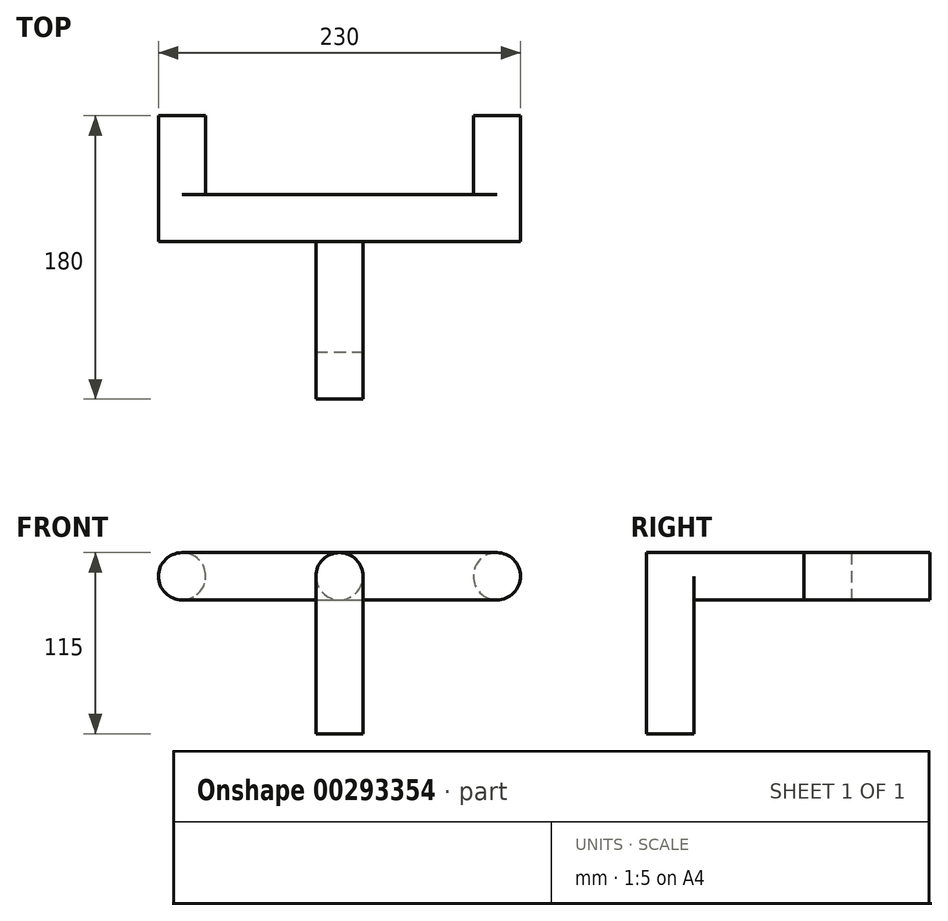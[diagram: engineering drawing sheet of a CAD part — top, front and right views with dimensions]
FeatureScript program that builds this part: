
annotation { "Feature Type Name" : "Feature", "Feature Type Description" : "" }
export const myFeature = defineFeature(function(context is Context, id is Id, definition is map)
    precondition{}
    {
        {
            var Q0;
            Q0=qCreatedBy(makeId("Front.planeOp"),FACE);
            cPlane(context, id + "F0", {"entities" : qUnion([Q0]), "cplaneType" : CPlaneType.OFFSET, "offset" : 50 * mm, "width" : 150 * mm, "height" : 150 * mm});
        }
        {
            var Q0;
            Q0=qCreatedBy(id+"F0.planeOp",FACE);
            var sketch = newSketch(context, id + "F1", { "sketchPlane" : qUnion([Q0])});
            skLineSegment(sketch, "E0", {"start": v(100, -14.73) * mm, "end": v(100, -15) * mm});
            skLineSegment(sketch, "E1.bottom", {"start": v(-100, 15) * mm, "end": v(100, 15) * mm});
            skLineSegment(sketch, "E1.top", {"start": v(-100, -15) * mm, "end": v(100, -15) * mm});
            skLineSegment(sketch, "E1.right", {"start": v(100, 15) * mm, "end": v(100, 14.73) * mm});
            skArc(sketch, "E2", {"start": v(-100, 15) * mm, "mid": v(-115, 0) * mm, "end": v(-100, -15) * mm});
            skArc(sketch, "E3", {"start": v(100, -14.73) * mm, "mid": v(114.73, 0) * mm, "end": v(100, 14.73) * mm});
            skArc(sketch, "E4", {"start": v(100, -15) * mm, "mid": v(115, 0) * mm, "end": v(100, 15) * mm});
            skLineSegment(sketch, "E5.top", {"start": v(-100, -14.73) * mm, "end": v(100, -14.73) * mm});
            skSolve(sketch);
        }
        {
            var Q0;
            Q0 = qSketchRegion(id + "F1", true);
            extrude(context, id + "F2", {"entities" : qUnion([Q0]), "depth" : 30 * mm});
        }
        {
            var Q0;
            Q0=makeQuery(id+"F2.opExtrude","CAP_FACE",FACE,{"disambiguationData":[OSD([sQuery(id+"F1.wireOp",EDGE,"E1.top"),sQuery(id+"F1.wireOp",EDGE,"E2"),sQuery(id+"F1.wireOp",EDGE,"E4"),sQuery(id+"F1.wireOp",EDGE,"E1.bottom")])],"isStart":false});
            var sketch = newSketch(context, id + "F3", { "sketchPlane" : qUnion([Q0])});
            skCircle(sketch, "E6", {"center": v(0, 0) * mm, "radius": 15 * mm});
            skSolve(sketch);
        }
        {
            var Q0;
            Q0 = qSketchRegion(id + "F3", true);
            extrude(context, id + "F4", {"entities" : qUnion([Q0]), "operationType" : NewBodyOperationType.ADD, "depth" : 100 * mm});
        }
        {
            var Q0;
            Q0=makeQuery(id+"F2.opExtrude","CAP_FACE",FACE,{"disambiguationData":[OSD([sQuery(id+"F1.wireOp",EDGE,"E1.top"),sQuery(id+"F1.wireOp",EDGE,"E2"),sQuery(id+"F1.wireOp",EDGE,"E4"),sQuery(id+"F1.wireOp",EDGE,"E1.bottom")])],"isStart":true});
            var sketch = newSketch(context, id + "F5", { "sketchPlane" : qUnion([Q0])});
            skLineSegment(sketch, "E7", {"start": v(0, 0) * mm, "end": v(100, 0) * mm});
            skLineSegment(sketch, "E8", {"start": v(0, 0) * mm, "end": v(-100, 0) * mm});
            skCircle(sketch, "E9", {"center": v(100, 0) * mm, "radius": 15 * mm});
            skCircle(sketch, "E10", {"center": v(-100, 0) * mm, "radius": 15 * mm});
            skSolve(sketch);
        }
        {
            var Q0;
            {var subQ0=sQuery(id+"F5.wireOp",EDGE,"E10");var subQ1=makeQuery(id+"F5.imprint","INTERSECT",VERTEX,{"derivedFrom":[makeQuery(id+"F2.opExtrude","CAP_EDGE",EDGE,{"disambiguationData":[OSD([sQuery(id+"F1.wireOp",EDGE,"E1.bottom")])],"isStart":true}),subQ0]});var subQ2=makeQuery(id+"F5.imprint","INTERSECT",VERTEX,{"derivedFrom":[sQuery(id+"F5.wireOp",EDGE,"E8"),subQ0]});Q0=makeQuery(id+"F5.imprint","IMPRINT",FACE,{"disambiguationData":[TD([[makeQuery(id+"F5.imprint","IMPRINT",EDGE,{"disambiguationData":[TD([[subQ1,1.0],[subQ2,-1.0]])],"derivedFrom":subQ0}),1.0]])]});}
            var Q1;
            {var subQ0=sQuery(id+"F5.wireOp",EDGE,"E9");var subQ1=makeQuery(id+"F5.imprint","INTERSECT",VERTEX,{"derivedFrom":[makeQuery(id+"F2.opExtrude","CAP_EDGE",EDGE,{"disambiguationData":[OSD([sQuery(id+"F1.wireOp",EDGE,"E1.top")])],"isStart":true}),subQ0]});var subQ2=makeQuery(id+"F5.imprint","INTERSECT",VERTEX,{"derivedFrom":[makeQuery(id+"F2.opExtrude","CAP_EDGE",EDGE,{"disambiguationData":[OSD([sQuery(id+"F1.wireOp",EDGE,"E1.bottom")])],"isStart":true}),subQ0]});Q1=makeQuery(id+"F5.imprint","IMPRINT",FACE,{"disambiguationData":[TD([[makeQuery(id+"F5.imprint","IMPRINT",EDGE,{"disambiguationData":[TD([[subQ1,1.0],[subQ2,-1.0]])],"derivedFrom":subQ0}),-1.0]])]});}
            extrude(context, id + "F6", {"entities" : qUnion([Q0, Q1]), "operationType" : NewBodyOperationType.ADD, "depth" : 50 * mm});
        }
        {
            var Q0;
            Q0=qCreatedBy(makeId("Top.planeOp"),FACE);
            var sketch = newSketch(context, id + "F7", { "sketchPlane" : qUnion([Q0])});
            skLineSegment(sketch, "E11", {"start": v(0, 0) * mm, "end": v(0, -180) * mm});
            skLineSegment(sketch, "E12", {"start": v(0, -180) * mm, "end": v(-15, -180) * mm});
            skLineSegment(sketch, "E13", {"start": v(-15, -180) * mm, "end": v(-15, -150) * mm});
            skLineSegment(sketch, "E14", {"start": v(-15, -150) * mm, "end": v(15, -150) * mm});
            skLineSegment(sketch, "E15.bottom", {"start": v(-15, -180) * mm, "end": v(15, -180) * mm});
            skLineSegment(sketch, "E15.right", {"start": v(15, -180) * mm, "end": v(15, -150) * mm});
            skSolve(sketch);
        }
        {
            var Q0;
            Q0 = qSketchRegion(id + "F7", true);
            extrude(context, id + "F8", {"entities" : qUnion([Q0]), "operationType" : NewBodyOperationType.ADD, "oppositeDirection" : true, "depth" : 100 * mm});
        }
    });
